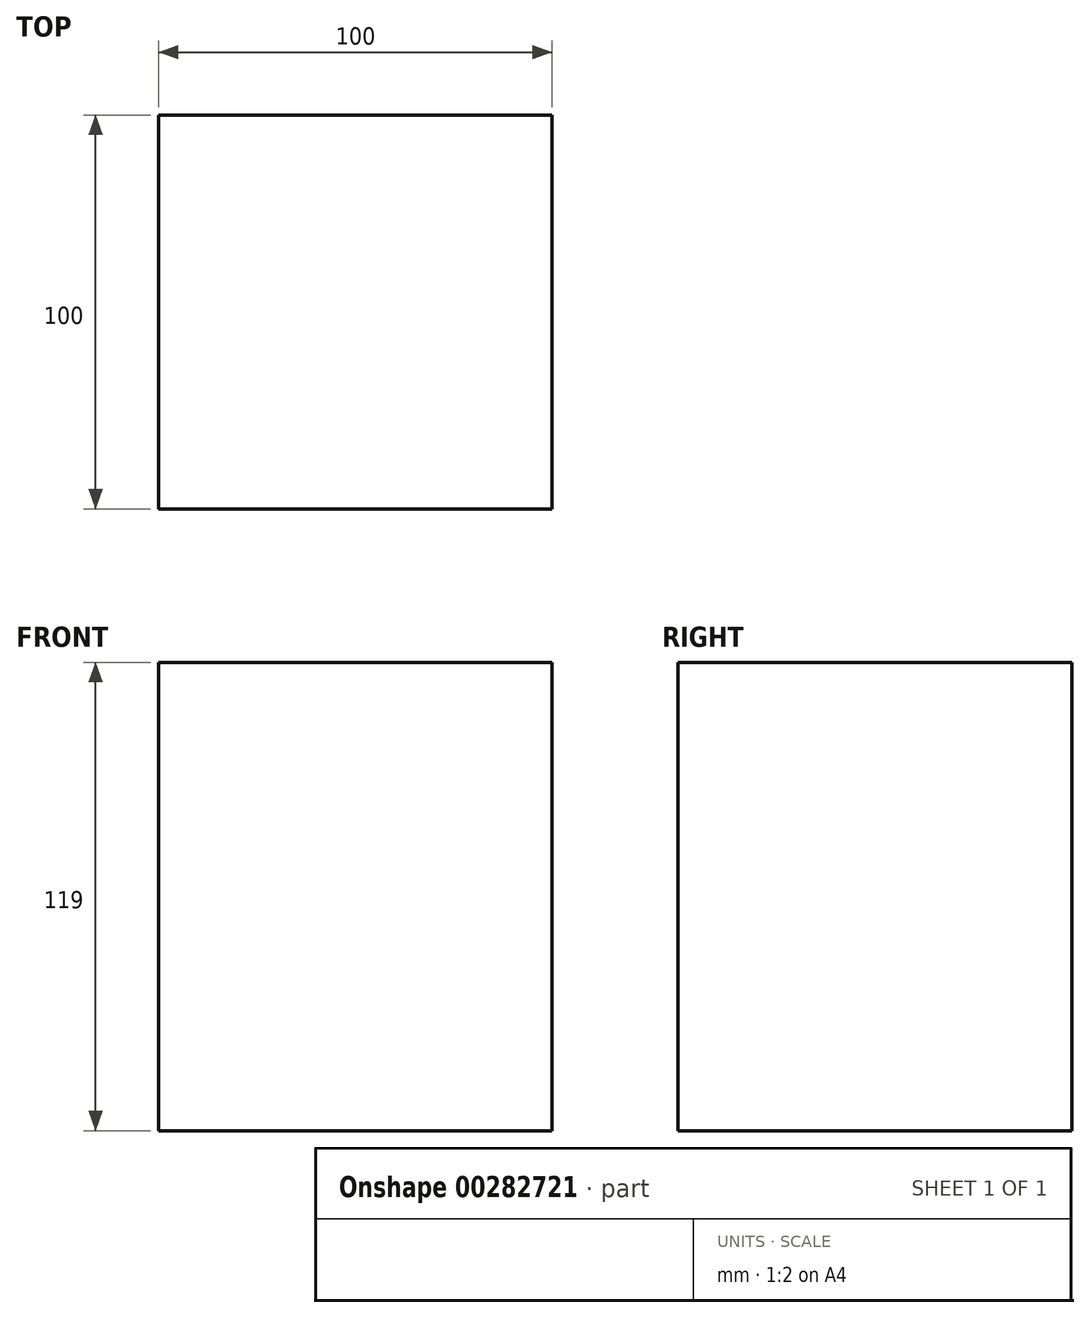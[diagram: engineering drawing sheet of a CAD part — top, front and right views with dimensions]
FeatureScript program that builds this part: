
annotation { "Feature Type Name" : "Feature", "Feature Type Description" : "" }
export const myFeature = defineFeature(function(context is Context, id is Id, definition is map)
    precondition{}
    {
        {
            var Q0;
            Q0=qCreatedBy(makeId("Top.planeOp"),FACE);
            var sketch = newSketch(context, id + "F0", { "sketchPlane" : qUnion([Q0])});
            skLineSegment(sketch, "E0.bottom", {"start": v(0, 0) * mm, "end": v(100, 0) * mm});
            skLineSegment(sketch, "E0.top", {"start": v(0, 100) * mm, "end": v(100, 100) * mm});
            skLineSegment(sketch, "E0.left", {"start": v(0, 0) * mm, "end": v(0, 100) * mm});
            skLineSegment(sketch, "E0.right", {"start": v(100, 0) * mm, "end": v(100, 100) * mm});
            skSolve(sketch);
        }
        {
            var Q0;
            Q0 = qSketchRegion(id + "F0", true);
            extrude(context, id + "F1", {"entities" : qUnion([Q0]), "oppositeDirection" : true, "depth" : 119 * mm});
        }
    });
